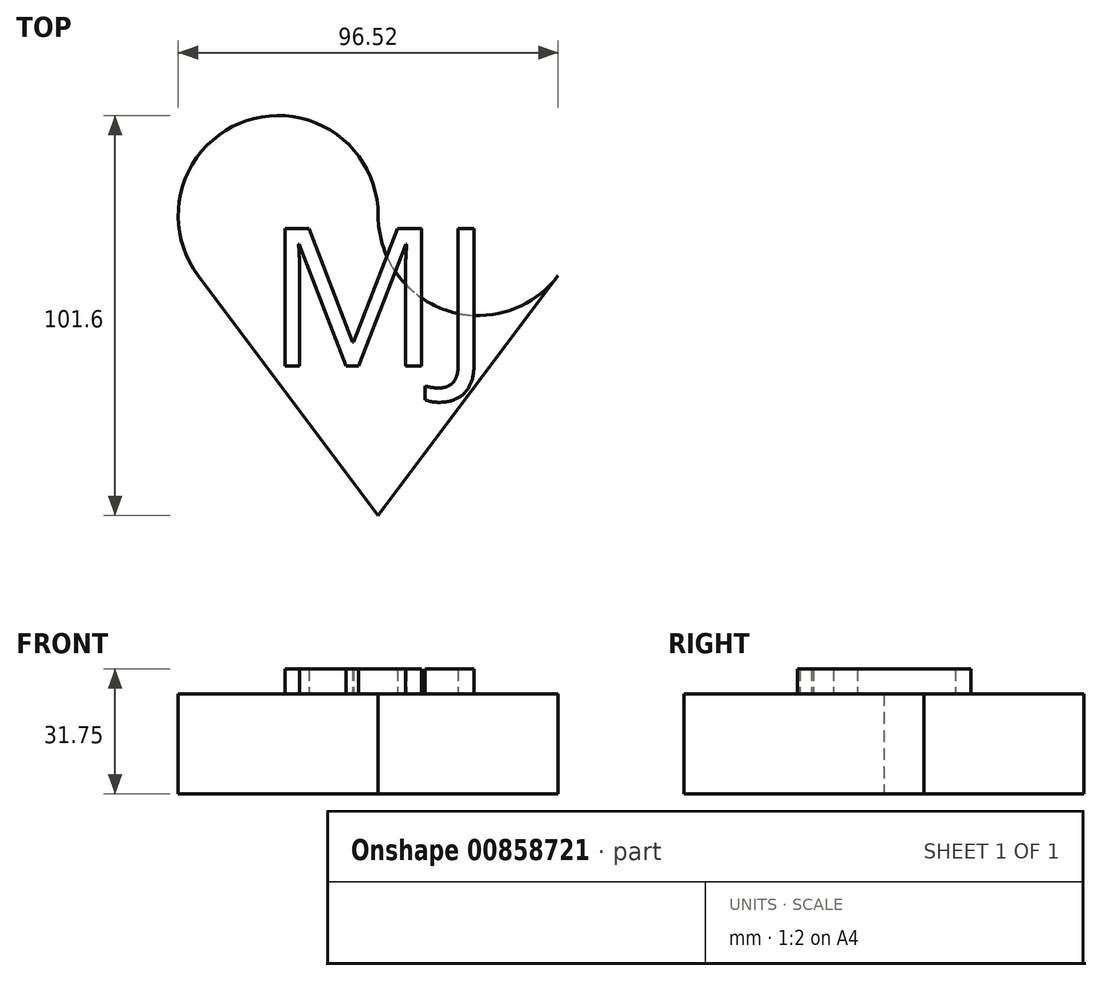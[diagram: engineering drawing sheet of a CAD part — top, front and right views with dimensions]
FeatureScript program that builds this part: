
annotation { "Feature Type Name" : "Feature", "Feature Type Description" : "" }
export const myFeature = defineFeature(function(context is Context, id is Id, definition is map)
    precondition{}
    {
        {
            var Q0;
            Q0=qCreatedBy(makeId("Top.planeOp"),FACE);
            var sketch = newSketch(context, id + "F0", { "sketchPlane" : qUnion([Q0])});
            skLineSegment(sketch, "E0", {"start": v(0, 0) * mm, "end": v(-25.4, 0) * mm});
            skLineSegment(sketch, "E1", {"start": v(-25.4, 0) * mm, "end": v(-25.4, 76.2) * mm});
            skLineSegment(sketch, "E2", {"start": v(-25.4, 76.2) * mm, "end": v(0, 76.2) * mm});
            skLineSegment(sketch, "E3", {"start": v(0, 76.2) * mm, "end": v(0, 0) * mm});
            skCircle(sketch, "E4", {"center": v(-25.4, 76.2) * mm, "radius": 25.4 * mm});
            skLineSegment(sketch, "E5", {"start": v(0, 0) * mm, "end": v(-45.72, 60.96) * mm});
            skCircle(sketch, "E6.MirrorC", {"center": v(25.4, 76.2) * mm, "radius": 25.4 * mm});
            skLineSegment(sketch, "E7.MirrorCS", {"start": v(0, 0) * mm, "end": v(45.72, 60.96) * mm});
            skSolve(sketch);
        }
        {
            var Q0;
            {var subQ0=sQuery(id+"F0.wireOp",EDGE,"E2");Q0=makeQuery(id+"F0.imprint","IMPRINT",FACE,{"disambiguationData":[TD([[makeQuery(id+"F0.imprint","IMPRINT",EDGE,{"derivedFrom":subQ0}),1.0]])]});}
            var Q1;
            {var subQ0=sQuery(id+"F0.wireOp",EDGE,"E6.MirrorC");var subQ2=makeQuery(id+"F0.imprint","INTERSECT",VERTEX,{"derivedFrom":[subQ0,sQuery(id+"F0.wireOp",EDGE,"E7.MirrorCS")]});Q1=makeQuery(id+"F0.imprint","IMPRINT",FACE,{"disambiguationData":[TD([[makeQuery(id+"F0.imprint","IMPRINT",EDGE,{"disambiguationData":[TD([[subQ2,1.0]])],"derivedFrom":subQ0}),-1.0]])]});}
            var Q2;
            {var subQ0=sQuery(id+"F0.wireOp",EDGE,"E3");Q2=makeQuery(id+"F0.imprint","IMPRINT",FACE,{"disambiguationData":[TD([[makeQuery(id+"F0.imprint","IMPRINT",EDGE,{"derivedFrom":subQ0}),1.0]])]});}
            var Q3;
            {var subQ0=sQuery(id+"F0.wireOp",EDGE,"E5");var subQ1=sQuery(id+"F0.wireOp",EDGE,"E1");var subQ2=makeQuery(id+"F0.imprint","INTERSECT",VERTEX,{"derivedFrom":[subQ1,subQ0]});Q3=makeQuery(id+"F0.imprint","IMPRINT",FACE,{"disambiguationData":[TD([[makeQuery(id+"F0.imprint","IMPRINT",EDGE,{"disambiguationData":[TD([[subQ2,-1.0]])],"derivedFrom":subQ1}),1.0]])]});}
            var Q4;
            {var subQ5=sQuery(id+"F0.wireOp",EDGE,"E3");Q4=makeQuery(id+"F0.imprint","IMPRINT",FACE,{"disambiguationData":[TD([[makeQuery(id+"F0.imprint","IMPRINT",EDGE,{"derivedFrom":subQ5}),-1.0]])]});}
            var Q5;
            {var subQ0=sQuery(id+"F0.wireOp",EDGE,"E2");Q5=makeQuery(id+"F0.imprint","IMPRINT",FACE,{"disambiguationData":[TD([[makeQuery(id+"F0.imprint","IMPRINT",EDGE,{"derivedFrom":subQ0}),-1.0]])]});}
            extrude(context, id + "F1", {"entities" : qUnion([Q0, Q1, Q2, Q3, Q4, Q5]), "depth" : 25.4 * mm, "offsetDistance" : 25.4 * mm});
        }
        {
            var Q0;
            Q0=makeQuery(id+"F1.opExtrude","CAP_FACE",FACE,{"disambiguationData":[OSD([sQuery(id+"F0.wireOp",EDGE,"E4"),sQuery(id+"F0.wireOp",EDGE,"E5"),sQuery(id+"F0.wireOp",EDGE,"E6.MirrorC"),sQuery(id+"F0.wireOp",EDGE,"E7.MirrorCS")])],"isStart":false});
            var sketch = newSketch(context, id + "F2", { "sketchPlane" : qUnion([Q0])});
            skText(sketch, "E8", { "text": "MJ", "fontName": "OpenSans-Regular.ttf"});
            const initialGuessF2  = {"E8": [-0.02847, 0.03796, 1, 0, 0.03526]};
            skSetInitialGuess(sketch, initialGuessF2);
            skSolve(sketch);
        }
        {
            var Q0;
            Q0 = qSketchRegion(id + "F2", true);
            extrude(context, id + "F3", {"entities" : qUnion([Q0]), "operationType" : NewBodyOperationType.ADD, "depth" : 6.35 * mm, "offsetDistance" : 25.4 * mm});
        }
    });
